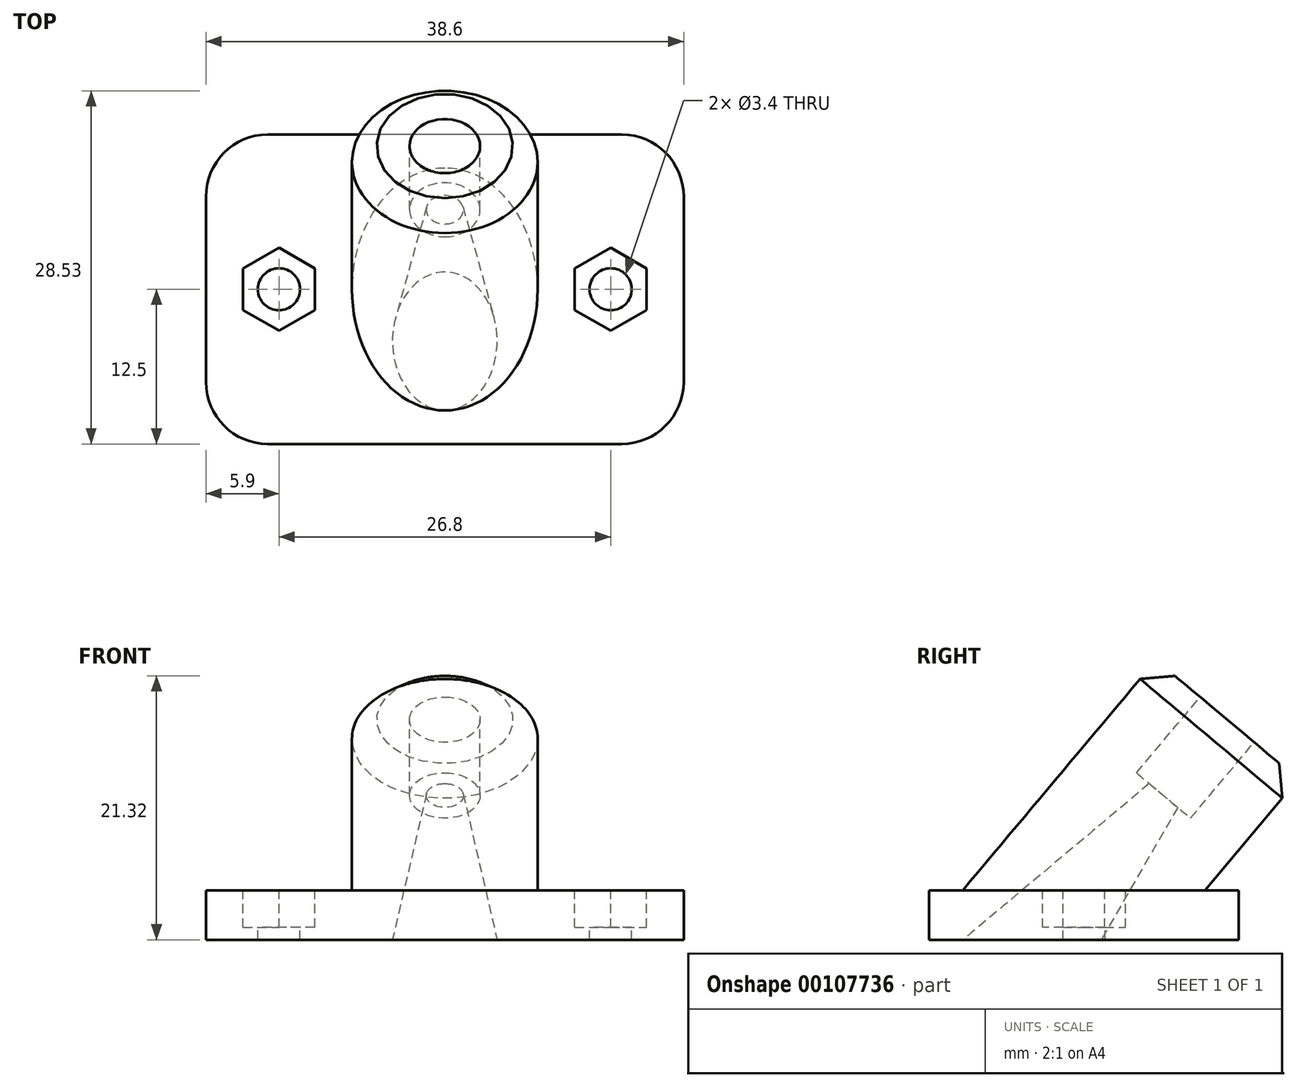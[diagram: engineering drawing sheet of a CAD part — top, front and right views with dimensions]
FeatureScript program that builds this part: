
annotation { "Feature Type Name" : "Feature", "Feature Type Description" : "" }
export const myFeature = defineFeature(function(context is Context, id is Id, definition is map)
    precondition{}
    {
        {
            var Q0;
            Q0=qCreatedBy(makeId("Top.planeOp"),FACE);
            var sketch = newSketch(context, id + "F0", { "sketchPlane" : qUnion([Q0])});
            skLineSegment(sketch, "E0.bottom", {"start": v(19.3, -12.5) * mm, "end": v(-19.3, -12.5) * mm});
            skLineSegment(sketch, "E0.top", {"start": v(19.3, 12.5) * mm, "end": v(-19.3, 12.5) * mm});
            skLineSegment(sketch, "E0.left", {"start": v(19.3, -12.5) * mm, "end": v(19.3, 12.5) * mm});
            skLineSegment(sketch, "E0.right", {"start": v(-19.3, -12.5) * mm, "end": v(-19.3, 12.5) * mm});
            skPoint(sketch, "E0.middle", {"position": v(0, 0) * mm});
            skLineSegment(sketch, "E1", {"start": v(-19.3, 0) * mm, "end": v(19.3, 0) * mm, "construction": true});
            skCircle(sketch, "E2", {"center": v(0, 0) * mm, "radius": 7.5 * mm, "construction": true});
            skCircle(sketch, "E3.cCircle", {"center": v(-13.4, 0) * mm, "radius": 2.9 * mm, "construction": true});
            skLineSegment(sketch, "E3.0", {"start": v(-10.5, -1.67) * mm, "end": v(-13.4, -3.35) * mm});
            skLineSegment(sketch, "E3.1", {"start": v(-13.4, -3.35) * mm, "end": v(-16.3, -1.67) * mm});
            skLineSegment(sketch, "E3.2", {"start": v(-16.3, -1.67) * mm, "end": v(-16.3, 1.67) * mm});
            skLineSegment(sketch, "E3.3", {"start": v(-16.3, 1.67) * mm, "end": v(-13.4, 3.35) * mm});
            skLineSegment(sketch, "E3.4", {"start": v(-13.4, 3.35) * mm, "end": v(-10.5, 1.67) * mm});
            skLineSegment(sketch, "E3.5", {"start": v(-10.5, 1.67) * mm, "end": v(-10.5, -1.67) * mm});
            skPoint(sketch, "E3.0.midPoint", {"position": v(-11.95, -2.51) * mm});
            skCircle(sketch, "E4", {"center": v(-13.4, 0) * mm, "radius": 1.7 * mm});
            skLineSegment(sketch, "E5", {"start": v(0, 12.5) * mm, "end": v(0, -12.5) * mm, "construction": true});
            skLineSegment(sketch, "E6.MirrorCS", {"start": v(10.5, -1.67) * mm, "end": v(13.4, -3.35) * mm});
            skLineSegment(sketch, "E7.MirrorCS", {"start": v(10.5, 1.67) * mm, "end": v(10.5, -1.67) * mm});
            skPoint(sketch, "E8.MirrorP", {"position": v(11.95, -2.51) * mm});
            skLineSegment(sketch, "E9.MirrorCS", {"start": v(13.4, -3.35) * mm, "end": v(16.3, -1.67) * mm});
            skLineSegment(sketch, "E10.MirrorCS", {"start": v(13.4, 3.35) * mm, "end": v(10.5, 1.67) * mm});
            skCircle(sketch, "E11.MirrorC", {"center": v(13.4, 0) * mm, "radius": 2.9 * mm, "construction": true});
            skLineSegment(sketch, "E12.MirrorCS", {"start": v(16.3, -1.67) * mm, "end": v(16.3, 1.67) * mm});
            skLineSegment(sketch, "E13.MirrorCS", {"start": v(16.3, 1.67) * mm, "end": v(13.4, 3.35) * mm});
            skCircle(sketch, "E14.MirrorC", {"center": v(13.4, 0) * mm, "radius": 1.7 * mm});
            skSolve(sketch);
        }
        {
            var Q0;
            Q0=makeQuery(id+"F0.imprint","IMPRINT",FACE,{"disambiguationData":[TD([[makeQuery(id+"F0.imprint","IMPRINT",EDGE,{"derivedFrom":sQuery(id+"F0.wireOp",EDGE,"E0.bottom")}),-1.0]])]});
            var Q1;
            Q1=makeQuery(id+"F0.imprint","IMPRINT",FACE,{"disambiguationData":[TD([[makeQuery(id+"F0.imprint","IMPRINT",EDGE,{"derivedFrom":sQuery(id+"F0.wireOp",EDGE,"E3.0")}),-1.0]])]});
            var Q2;
            Q2=makeQuery(id+"F0.imprint","IMPRINT",FACE,{"disambiguationData":[TD([[makeQuery(id+"F0.imprint","IMPRINT",EDGE,{"derivedFrom":sQuery(id+"F0.wireOp",EDGE,"E6.MirrorCS")}),1.0]])]});
            extrude(context, id + "F1", {"entities" : qUnion([Q0, Q1, Q2]), "oppositeDirection" : true, "depth" : 4 * mm});
        }
        {
            var Q0;
            Q0=makeQuery(id+"F1.opExtrude","SWEPT_EDGE",EDGE,{"disambiguationData":[OSD([sQuery(id+"F0.wireOp",EDGE,"E0.top"),sQuery(id+"F0.wireOp",EDGE,"E0.right")])]});
            var Q1;
            Q1=makeQuery(id+"F1.opExtrude","SWEPT_EDGE",EDGE,{"disambiguationData":[OSD([sQuery(id+"F0.wireOp",EDGE,"E0.top"),sQuery(id+"F0.wireOp",EDGE,"E0.left")])]});
            var Q2;
            Q2=makeQuery(id+"F1.opExtrude","SWEPT_EDGE",EDGE,{"disambiguationData":[OSD([sQuery(id+"F0.wireOp",EDGE,"E0.bottom"),sQuery(id+"F0.wireOp",EDGE,"E0.left")])]});
            var Q3;
            Q3=makeQuery(id+"F1.opExtrude","SWEPT_EDGE",EDGE,{"disambiguationData":[OSD([sQuery(id+"F0.wireOp",EDGE,"E0.bottom"),sQuery(id+"F0.wireOp",EDGE,"E0.right")])]});
            fillet(context, id + "F2", {"entities" : qUnion([Q0, Q1, Q2, Q3]), "radius" : 5 * mm, "tangentPropagation" : true, "allowEdgeOverflow" : false});
        }
        {
            var Q0;
            Q0=makeQuery(id+"F0.imprint","IMPRINT",FACE,{"disambiguationData":[TD([[makeQuery(id+"F0.imprint","IMPRINT",EDGE,{"derivedFrom":sQuery(id+"F0.wireOp",EDGE,"E3.0")}),-1.0]])]});
            var Q1;
            Q1=makeQuery(id+"F0.imprint","IMPRINT",FACE,{"disambiguationData":[TD([[makeQuery(id+"F0.imprint","IMPRINT",EDGE,{"derivedFrom":sQuery(id+"F0.wireOp",EDGE,"E6.MirrorCS")}),1.0]])]});
            extrude(context, id + "F3", {"entities" : qUnion([Q0, Q1]), "operationType" : NewBodyOperationType.REMOVE, "oppositeDirection" : true, "depth" : 3 * mm});
        }
        {
            var Q0;
            Q0=sQuery(id+"F0.wireOp",EDGE,"E1");
            cPlane(context, id + "F4", {"entities" : qUnion([Q0]), "cplaneType" : CPlaneType.LINE_ANGLE, "offset" : 150 * mm, "angle" : 50 * degree, "width" : 150 * mm, "height" : 150 * mm});
        }
        {
            var Q0;
            Q0=qCreatedBy(id+"F4.planeOp",FACE);
            var sketch = newSketch(context, id + "F5", { "sketchPlane" : qUnion([Q0])});
            skCircle(sketch, "E15", {"center": v(0, 0) * mm, "radius": 7.5 * mm});
            skSolve(sketch);
        }
        {
            var Q0;
            Q0=qSketchRegion(id+"F5",true);
            var Q1;
            Q1=makeQuery(id+"F1.opExtrude","CAP_FACE",FACE,{"disambiguationData":[OSD([sQuery(id+"F0.wireOp",EDGE,"E0.bottom"),sQuery(id+"F0.wireOp",EDGE,"E0.top"),sQuery(id+"F0.wireOp",EDGE,"E0.left"),sQuery(id+"F0.wireOp",EDGE,"E0.right"),sQuery(id+"F0.wireOp",EDGE,"E4"),sQuery(id+"F0.wireOp",EDGE,"E14.MirrorC")])],"isStart":true});
            extrude(context, id + "F6", {"entities" : qUnion([Q0]), "operationType" : NewBodyOperationType.ADD, "endBound" : BoundingType.UP_TO_SURFACE, "oppositeDirection" : true, "endBoundEntityFace" : qUnion([Q1]), "depth" : 25 * mm, "hasSecondDirection" : true, "secondDirectionOppositeDirection" : false, "secondDirectionDepth" : 18 * mm});
        }
        {
            var Q0;
            Q0=makeQuery(id+"F6.opExtrude","CAP_FACE",FACE,{"disambiguationData":[OSD([sQuery(id+"F5.wireOp",EDGE,"E15")])],"isStart":true});
            var sketch = newSketch(context, id + "F7", { "sketchPlane" : qUnion([Q0])});
            skCircle(sketch, "E16", {"center": v(0, 0) * mm, "radius": 2.85 * mm});
            skSolve(sketch);
        }
        {
            var Q0;
            Q0=qSketchRegion(id+"F7",true);
            extrude(context, id + "F8", {"entities" : qUnion([Q0]), "operationType" : NewBodyOperationType.REMOVE, "oppositeDirection" : true, "depth" : 8 * mm});
        }
        {
            var Q0;
            Q0=makeQuery(id+"F8.boolean.opBoolean","COPY",FACE,{"derivedFrom":makeQuery(id+"F8.opExtrude","CAP_FACE",FACE,{"disambiguationData":[OSD([sQuery(id+"F7.wireOp",EDGE,"E16")])],"isStart":false})});
            var sketch = newSketch(context, id + "F9", { "sketchPlane" : qUnion([Q0])});
            skCircle(sketch, "E17", {"center": v(0, 0) * mm, "radius": 1.5 * mm});
            skSolve(sketch);
        }
        {
            var Q0;
            Q0=qSketchRegion(id+"F9",true);
            var Q1;
            Q1=makeQuery(id+"F1.opExtrude","CAP_FACE",FACE,{"disambiguationData":[OSD([sQuery(id+"F0.wireOp",EDGE,"E0.bottom"),sQuery(id+"F0.wireOp",EDGE,"E0.top"),sQuery(id+"F0.wireOp",EDGE,"E0.left"),sQuery(id+"F0.wireOp",EDGE,"E0.right"),sQuery(id+"F0.wireOp",EDGE,"E4"),sQuery(id+"F0.wireOp",EDGE,"E14.MirrorC")])],"isStart":false});
            extrude(context, id + "F10", {"entities" : qUnion([Q0]), "operationType" : NewBodyOperationType.REMOVE, "endBound" : BoundingType.UP_TO_SURFACE, "oppositeDirection" : true, "endBoundEntityFace" : qUnion([Q1]), "depth" : 25 * mm, "hasDraft" : true, "draftAngle" : 10 * degree});
        }
        {
            var Q0;
            Q0=makeQuery(id+"F6.opExtrude","CAP_EDGE",EDGE,{"disambiguationData":[OSD([sQuery(id+"F5.wireOp",EDGE,"E15")])],"isStart":true});
            chamfer(context, id + "F11", {"entities" : qUnion([Q0]), "width" : 2 * mm, "tangentPropagation" : true});
        }
    });
